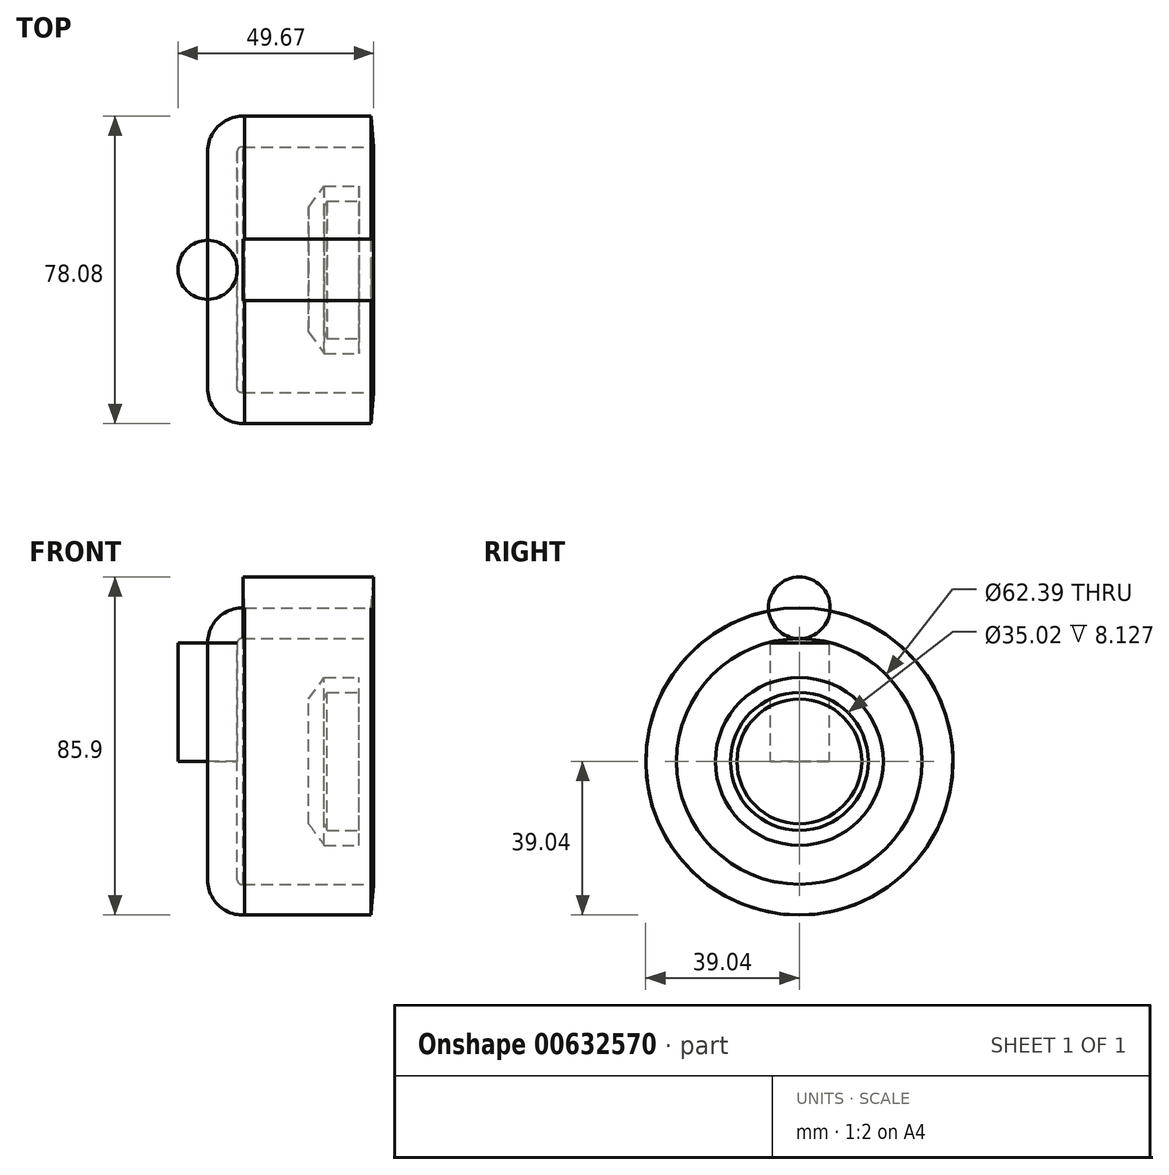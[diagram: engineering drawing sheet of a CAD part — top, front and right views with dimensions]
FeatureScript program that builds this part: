
annotation { "Feature Type Name" : "Feature", "Feature Type Description" : "" }
export const myFeature = defineFeature(function(context is Context, id is Id, definition is map)
    precondition{}
    {
        {
            var Q0;
            Q0=qCreatedBy(makeId("Front.planeOp"),FACE);
            var sketch = newSketch(context, id + "F0", { "sketchPlane" : qUnion([Q0])});
            skLineSegment(sketch, "E0", {"start": v(0, 0) * mm, "end": v(0, 30.09) * mm});
            skArc(sketch, "E1", {"start": v(9.42, 39.02) * mm, "mid": v(2.79, 36.58) * mm, "end": v(0, 30.09) * mm});
            skLineSegment(sketch, "E2", {"start": v(9.42, 39.02) * mm, "end": v(41.45, 39.02) * mm});
            skLineSegment(sketch, "E3", {"start": v(7.5, 0) * mm, "end": v(7.5, 30.07) * mm});
            skArc(sketch, "E4", {"start": v(9.03, 31.2) * mm, "mid": v(7.98, 31.02) * mm, "end": v(7.5, 30.07) * mm});
            skLineSegment(sketch, "E5", {"start": v(9.03, 31.2) * mm, "end": v(42.16, 31.2) * mm});
            skLineSegment(sketch, "E6", {"start": v(41.45, 39.02) * mm, "end": v(42.16, 31.2) * mm});
            skLineSegment(sketch, "E7", {"start": v(7.5, 0) * mm, "end": v(0, 0) * mm});
            skLineSegment(sketch, "E8", {"start": v(7.5, 30.07) * mm, "end": v(0, 30.09) * mm});
            skLineSegment(sketch, "E9", {"start": v(9.42, 39.02) * mm, "end": v(9.03, 31.2) * mm});
            skLineSegment(sketch, "E10.MirrorCS", {"start": v(9.03, 46.86) * mm, "end": v(42.16, 46.86) * mm});
            skLineSegment(sketch, "E11.MirrorCS", {"start": v(-7.5, 0) * mm, "end": v(-7.5, 30.07) * mm});
            skArc(sketch, "E12", {"start": v(9.03, 46.86) * mm, "mid": v(-2.75, 41.93) * mm, "end": v(-7.5, 30.07) * mm});
            skLineSegment(sketch, "E13", {"start": v(-20.24, 0) * mm, "end": v(25.68, 0) * mm});
            skLineSegment(sketch, "E14", {"start": v(25.68, 0) * mm, "end": v(25.68, 15.86) * mm});
            skLineSegment(sketch, "E15", {"start": v(25.68, 15.86) * mm, "end": v(29.62, 21.3) * mm});
            skLineSegment(sketch, "E16", {"start": v(29.62, 21.3) * mm, "end": v(38.49, 21.3) * mm});
            skLineSegment(sketch, "E17", {"start": v(38.49, 21.3) * mm, "end": v(38.49, 17.5) * mm});
            skLineSegment(sketch, "E18", {"start": v(38.49, 17.5) * mm, "end": v(30.36, 17.5) * mm});
            skLineSegment(sketch, "E19", {"start": v(30.36, 17.5) * mm, "end": v(29.62, 15.86) * mm});
            skLineSegment(sketch, "E20", {"start": v(29.62, 15.86) * mm, "end": v(29.62, 0) * mm});
            skLineSegment(sketch, "E21", {"start": v(29.62, 0) * mm, "end": v(25.68, 0) * mm});
            skSolve(sketch);
        }
        {
            var Q0;
            Q0=makeQuery(id+"F0.imprint","IMPRINT",FACE,{"disambiguationData":[TD([[makeQuery(id+"F0.imprint","IMPRINT",EDGE,{"derivedFrom":sQuery(id+"F0.wireOp",EDGE,"E0")}),-1.0]])]});
            var Q1;
            Q1=sQuery(id+"F0.wireOp",EDGE,"E0");
            revolve(context, id + "F1", {"surfaceOperationType" : NewSurfaceOperationType.NEW, "entities" : qUnion([Q0]), "axis" : qUnion([Q1]), "revolveType" : RevolveType.FULL});
        }
        {
            var Q0;
            Q0=makeQuery(id+"F0.imprint","IMPRINT",FACE,{"disambiguationData":[TD([[makeQuery(id+"F0.imprint","IMPRINT",EDGE,{"derivedFrom":sQuery(id+"F0.wireOp",EDGE,"E2")}),-1.0]])]});
            var Q1;
            Q1=sQuery(id+"F0.wireOp",EDGE,"E2");
            revolve(context, id + "F2", {"surfaceOperationType" : NewSurfaceOperationType.NEW, "entities" : qUnion([Q0]), "axis" : qUnion([Q1]), "revolveType" : RevolveType.FULL});
        }
        {
            var Q0;
            Q0=sQuery(id+"F0.wireOp",EDGE,"E12");
            var Q1;
            Q1=makeQuery(id+"F2.opRevolve","SWEPT_FACE",FACE,{"disambiguationData":[OSD([sQuery(id+"F0.wireOp",EDGE,"E9")])]});
            var Q2;
            Q2=makeQuery(id+"F1.opRevolve","SWEPT_FACE",FACE,{"disambiguationData":[OSD([sQuery(id+"F0.wireOp",EDGE,"E8")])]});
            var Q3;
            Q3=sQuery(id+"F0.wireOp",EDGE,"E12");
            var Q4;
            Q4=sQuery(id+"F0.wireOp",EDGE,"E4");
            loft(context, id + "F3", {"bodyType" : ToolBodyType.SURFACE, "spine" : qUnion([Q0]), "addGuides" : true, "wireProfilesArray" : [{ "wireProfileEntities" : qUnion([Q1]) }, { "wireProfileEntities" : qUnion([Q2]) }], "guidesArray" : [{ "guideEntities" : qUnion([Q3]), "guideDerivativeType" : LoftGuideDerivativeType.DEFAULT, "guideDerivativeMagnitude" : 1 }, { "guideEntities" : qUnion([Q4]), "guideDerivativeType" : LoftGuideDerivativeType.DEFAULT, "guideDerivativeMagnitude" : 1 }]});
        }
        {
            var Q0;
            {Q0=qUnion([makeQuery(id+"F0.imprint","IMPRINT",FACE,{"disambiguationData":[TD([[makeQuery(id+"F0.imprint","IMPRINT",EDGE,{"derivedFrom":sQuery(id+"F0.wireOp",EDGE,"E14")}),-1.0]])]}),makeQuery(id+"F0.imprint","IMPRINT",FACE,{"disambiguationData":[TD([[makeQuery(id+"F0.imprint","IMPRINT",EDGE,{"derivedFrom":sQuery(id+"F0.wireOp",EDGE,"E0")}),-1.0]])]}),makeQuery(id+"F0.imprint","IMPRINT",FACE,{"disambiguationData":[TD([[makeQuery(id+"F0.imprint","IMPRINT",EDGE,{"derivedFrom":sQuery(id+"F0.wireOp",EDGE,"E2")}),-1.0]])]}),makeQuery(id+"F0.imprint","IMPRINT",FACE,{"disambiguationData":[TD([[makeQuery(id+"F0.imprint","IMPRINT",EDGE,{"derivedFrom":sQuery(id+"F0.wireOp",EDGE,"E1")}),1.0]])]})]);}
            var Q1;
            Q1=sQuery(id+"F0.wireOp",EDGE,"E21");
            revolve(context, id + "F4", {"surfaceOperationType" : NewSurfaceOperationType.NEW, "entities" : qUnion([Q0]), "axis" : qUnion([Q1]), "revolveType" : RevolveType.FULL});
        }
    });
